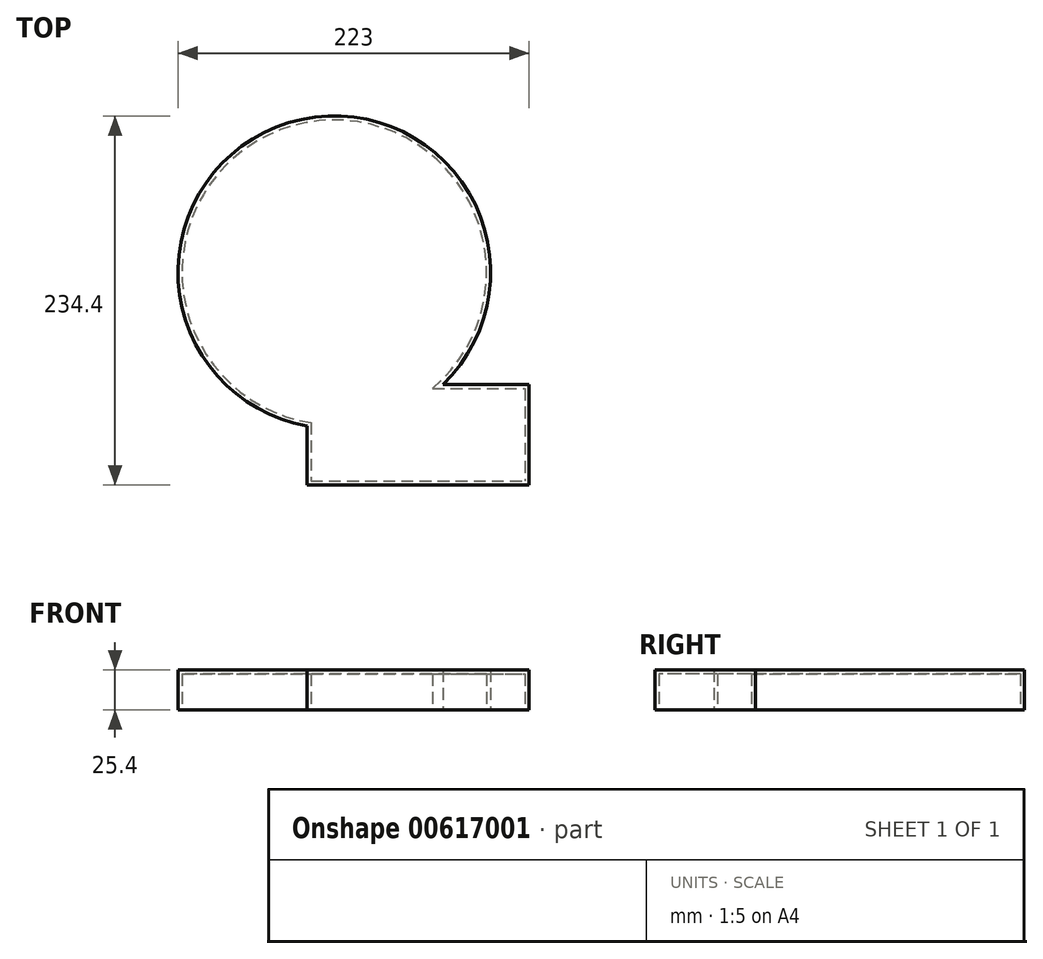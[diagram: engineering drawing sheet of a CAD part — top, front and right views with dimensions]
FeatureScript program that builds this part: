
annotation { "Feature Type Name" : "Feature", "Feature Type Description" : "" }
export const myFeature = defineFeature(function(context is Context, id is Id, definition is map)
    precondition{}
    {
        {
            var Q0;
            Q0=qCreatedBy(makeId("Top.planeOp"),FACE);
            var sketch = newSketch(context, id + "F0", { "sketchPlane" : qUnion([Q0])});
            skLineSegment(sketch, "E0.bottom", {"start": v(-121.95, 7.6) * mm, "end": v(19.23, 7.6) * mm});
            skLineSegment(sketch, "E0.top", {"start": v(-121.95, -56.15) * mm, "end": v(19.23, -56.15) * mm});
            skLineSegment(sketch, "E0.left", {"start": v(-121.95, 7.6) * mm, "end": v(-121.95, -56.15) * mm});
            skLineSegment(sketch, "E0.right", {"start": v(19.23, 7.6) * mm, "end": v(19.23, -56.15) * mm});
            skCircle(sketch, "E1", {"center": v(-104.52, 79) * mm, "radius": 99.25 * mm});
            skSolve(sketch);
        }
        {
            var Q0;
            {var subQ2=sQuery(id+"F0.wireOp",EDGE,"E0.top");Q0=makeQuery(id+"F0.imprint","IMPRINT",FACE,{"disambiguationData":[TD([[makeQuery(id+"F0.imprint","IMPRINT",EDGE,{"derivedFrom":subQ2}),1.0]])]});}
            var Q1;
            {var subQ0=sQuery(id+"F0.wireOp",EDGE,"E0.left");var subQ1=sQuery(id+"F0.wireOp",EDGE,"E0.bottom");var subQ2=makeQuery(id+"F0.imprint","INTERSECT",VERTEX,{"derivedFrom":[subQ1,subQ0]});Q1=makeQuery(id+"F0.imprint","IMPRINT",FACE,{"disambiguationData":[TD([[makeQuery(id+"F0.imprint","IMPRINT",EDGE,{"disambiguationData":[TD([[subQ2,-1.0]])],"derivedFrom":subQ1}),-1.0]])]});}
            var Q2;
            {var subQ0=sQuery(id+"F0.wireOp",EDGE,"E0.left");var subQ1=sQuery(id+"F0.wireOp",EDGE,"E0.bottom");var subQ2=makeQuery(id+"F0.imprint","INTERSECT",VERTEX,{"derivedFrom":[subQ1,subQ0]});Q2=makeQuery(id+"F0.imprint","IMPRINT",FACE,{"disambiguationData":[TD([[makeQuery(id+"F0.imprint","IMPRINT",EDGE,{"disambiguationData":[TD([[subQ2,-1.0]])],"derivedFrom":subQ1}),1.0]])]});}
            extrude(context, id + "F1", {"entities" : qUnion([Q0, Q1, Q2]), "depth" : 25.4 * mm, "offsetDistance" : 25.4 * mm});
        }
        {
            var Q0;
            Q0=makeQuery(id+"F1.opExtrude","CAP_FACE",FACE,{"disambiguationData":[OSD([sQuery(id+"F0.wireOp",EDGE,"E0.bottom"),sQuery(id+"F0.wireOp",EDGE,"E0.top"),sQuery(id+"F0.wireOp",EDGE,"E0.left"),sQuery(id+"F0.wireOp",EDGE,"E0.right"),sQuery(id+"F0.wireOp",EDGE,"E1")])],"isStart":false});
            var sketch = newSketch(context, id + "F2", { "sketchPlane" : qUnion([Q0])});
            skCircle(sketch, "E2", {"center": v(-161.67, 76.9) * mm, "radius": 87.31 * mm});
            skSolve(sketch);
        }
        {
            var Q0;
            {var subQ0=sQuery(id+"F2.wireOp",EDGE,"E2");var subQ1=makeQuery(id+"F1.opExtrude","CAP_EDGE",EDGE,{"disambiguationData":[OSD([sQuery(id+"F0.wireOp",EDGE,"E1")])],"isStart":false});var subQ2=makeQuery(id+"F2.imprint","INTERSECT",VERTEX,{"disambiguationData":[OD(0.0)],"derivedFrom":[subQ1,subQ0]});Q0=makeQuery(id+"F2.imprint","IMPRINT",FACE,{"disambiguationData":[TD([[makeQuery(id+"F2.imprint","IMPRINT",EDGE,{"disambiguationData":[TD([[subQ2,1.0]])],"derivedFrom":subQ0}),1.0]])]});}
            extrude(context, id + "F3", {"entities" : qUnion([Q0]), "operationType" : NewBodyOperationType.ADD, "oppositeDirection" : true, "depth" : 25.4 * mm, "offsetDistance" : 25.4 * mm});
        }
        {
            var Q0;
            Q0=makeQuery(id+"F1.opExtrude","CAP_FACE",FACE,{"disambiguationData":[OSD([sQuery(id+"F0.wireOp",EDGE,"E0.bottom"),sQuery(id+"F0.wireOp",EDGE,"E0.top"),sQuery(id+"F0.wireOp",EDGE,"E0.left"),sQuery(id+"F0.wireOp",EDGE,"E0.right"),sQuery(id+"F0.wireOp",EDGE,"E1")])],"isStart":true});
            shell(context, id + "F4", {"entities" : qUnion([Q0]), "thickness" : 2.54 * mm});
        }
    });
